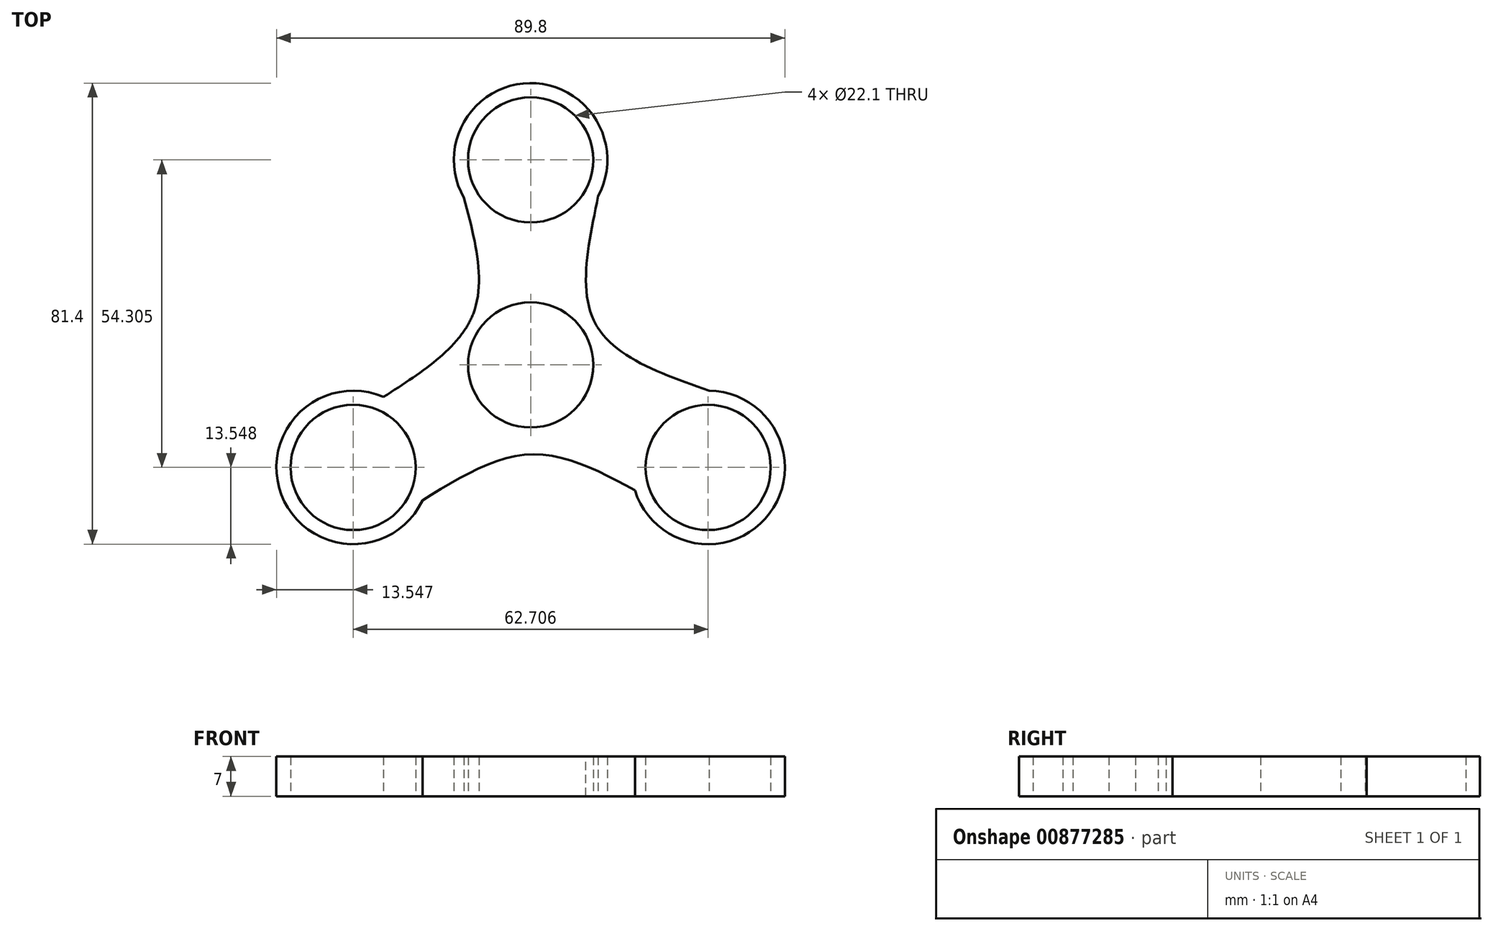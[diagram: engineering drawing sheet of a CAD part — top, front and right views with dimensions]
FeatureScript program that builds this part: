
annotation { "Feature Type Name" : "Feature", "Feature Type Description" : "" }
export const myFeature = defineFeature(function(context is Context, id is Id, definition is map)
    precondition{}
    {
        {
            var Q0;
            Q0=qCreatedBy(makeId("Top.planeOp"),FACE);
            var sketch = newSketch(context, id + "F0", { "sketchPlane" : qUnion([Q0])});
            skCircle(sketch, "E0", {"center": v(0, 0) * mm, "radius": 11.05 * mm});
            skCircle(sketch, "E1", {"center": v(0, 0) * mm, "radius": 13.55 * mm});
            skCircle(sketch, "E2", {"center": v(0, 36.2) * mm, "radius": 11.05 * mm});
            skCircle(sketch, "E3", {"center": v(0, 36.2) * mm, "radius": 13.55 * mm});
            skCircle(sketch, "E4.1.0", {"center": v(-31.35, -18.1) * mm, "radius": 11.05 * mm});
            skCircle(sketch, "E4.1.1", {"center": v(-31.35, -18.1) * mm, "radius": 13.55 * mm});
            skCircle(sketch, "E4.2.0", {"center": v(31.35, -18.1) * mm, "radius": 11.05 * mm});
            skCircle(sketch, "E4.2.1", {"center": v(31.35, -18.1) * mm, "radius": 13.55 * mm});
            skFitSpline(sketch, "E5", {"points": [v(-11.77, 29.49) * mm, v(-10.16, 8.96) * mm, v(-26, -5.65) * mm], "startDerivative": vector(11.95, -44.53) * mm, "endDerivative": vector(-40.05, -25.76) * mm});
            skFitSpline(sketch, "E6", {"points": [v(-19.1, -23.9) * mm, v(0, -15.78) * mm, v(18.41, -22.12) * mm], "startDerivative": vector(37.63, 23.33) * mm, "endDerivative": vector(37, -20.15) * mm});
            skFitSpline(sketch, "E7", {"points": [v(11.93, 29.78) * mm, v(11.53, 7.12) * mm, v(31.5, -4.55) * mm], "startDerivative": vector(-10.8, -51.01) * mm, "endDerivative": vector(49.8, -17.5) * mm});
            skSolve(sketch);
        }
        {
            var Q0;
            {var subQ0=sQuery(id+"F0.wireOp",EDGE,"E7");var subQ1=sQuery(id+"F0.wireOp",EDGE,"E1");var subQ2=makeQuery(id+"F0.imprint","INTERSECT",VERTEX,{"disambiguationData":[OD(0.0)],"derivedFrom":[subQ1,subQ0]});Q0=makeQuery(id+"F0.imprint","IMPRINT",FACE,{"disambiguationData":[TD([[makeQuery(id+"F0.imprint","IMPRINT",EDGE,{"disambiguationData":[TD([[subQ2,-1.0]])],"derivedFrom":subQ1}),-1.0]])]});}
            var Q1;
            Q1=makeQuery(id+"F0.imprint","IMPRINT",FACE,{"disambiguationData":[TD([[makeQuery(id+"F0.imprint","IMPRINT",EDGE,{"derivedFrom":sQuery(id+"F0.wireOp",EDGE,"E2")}),-1.0]])]});
            var Q2;
            Q2=makeQuery(id+"F0.imprint","IMPRINT",FACE,{"disambiguationData":[TD([[makeQuery(id+"F0.imprint","IMPRINT",EDGE,{"derivedFrom":sQuery(id+"F0.wireOp",EDGE,"E4.2.0")}),-1.0]])]});
            var Q3;
            {var subQ5=sQuery(id+"F0.wireOp",EDGE,"E6");Q3=makeQuery(id+"F0.imprint","IMPRINT",FACE,{"disambiguationData":[TD([[makeQuery(id+"F0.imprint","IMPRINT",EDGE,{"derivedFrom":subQ5}),1.0]])]});}
            var Q4;
            Q4=makeQuery(id+"F0.imprint","IMPRINT",FACE,{"disambiguationData":[TD([[makeQuery(id+"F0.imprint","IMPRINT",EDGE,{"derivedFrom":sQuery(id+"F0.wireOp",EDGE,"E4.1.0")}),-1.0]])]});
            var Q5;
            Q5=makeQuery(id+"F0.imprint","IMPRINT",FACE,{"disambiguationData":[TD([[makeQuery(id+"F0.imprint","IMPRINT",EDGE,{"derivedFrom":sQuery(id+"F0.wireOp",EDGE,"E0")}),-1.0]])]});
            extrude(context, id + "F1", {"entities" : qUnion([Q0, Q1, Q2, Q3, Q4, Q5]), "depth" : 7 * mm, "offsetDistance" : 25 * mm});
        }
    });
